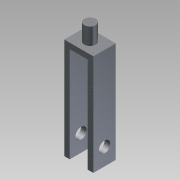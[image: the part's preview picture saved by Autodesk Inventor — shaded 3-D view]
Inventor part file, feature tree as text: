
AUTODESK INVENTOR PART (.ipt)
format: ipt  version: 2013 (Build 170138000, 138)  size: 105,984 bytes
history: native  units: in
note: dims shown in document units (in); Inventor stores cm internally (conversion verified against a paired STEP export)
features: extrude x3, sketch x3
ambient origin geometry x8: Origin, YZ Plane, XZ Plane, XY Plane, X Axis, Y Axis, Z Axis, Center Point
bodies: Solid1 (feature_tree)
feature tree (6):
  extrude  "Extrusion1"  Depth=4.5in
  extrude  "Extrusion2"  Depth=0.25in
  extrude  "Extrusion3"  Depth=1.0in TaperAngle=0.0deg
  sketch  "Sketch1"  dims[d0=1.3in d1=4.5in]
  sketch  "Sketch2"  dims[d2=0.25in d3=0.25in]
  sketch  "Sketch3"  dims[d4=0.25in d5=1.0in d6=0.0in d7=0.75in d8=0.5in d9=10.0in d10=0.0in d11=4.5in d12=0.5in d13=0.75in d14=0.0in]
